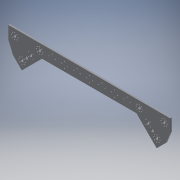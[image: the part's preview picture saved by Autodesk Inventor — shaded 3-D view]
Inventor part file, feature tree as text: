
AUTODESK INVENTOR PART (.ipt)
format: ipt  version: 2016 (Build 200138000, 138)  size: 222,720 bytes
history: native  units: mm
features: reference x28, extrude x1, sketch x1
ambient origin geometry x8: Origin, YZ Plane, XZ Plane, XY Plane, X Axis, Y Axis, Z Axis, Center Point
bodies: Body1 (feature_tree)
feature tree (30):
  extrude  "Extrusion3"  [1 undecoded]
  sketch  "Sketch1"  dims[d4=4.0mm d5=0.0mm]
  reference  "Reference2"
  reference  "Reference3"
  reference  "Reference4"
  reference  "Reference5"
  reference  "Reference6"
  reference  "Reference7"
  reference  "Reference8"
  reference  "Reference9"
  reference  "Reference10"
  reference  "Reference11"
  reference  "Reference12"
  reference  "Reference13"
  reference  "Reference14"
  reference  "Reference15"
  reference  "Reference16"
  reference  "Reference17"
  reference  "Reference18"
  reference  "Reference19"
  reference  "Reference20"
  reference  "Reference25"
  reference  "Reference26"
  reference  "Reference27"
  reference  "Reference28"
  reference  "Reference29"
  reference  "Reference30"
  reference  "Reference31"
  reference  "Reference32"
  reference  "Reference33"
note: 1 required parameter value undecoded (feature->parameter linkage not recoverable at this tier; creation-order binding heuristic only, values carry confidence <= 0.55)
